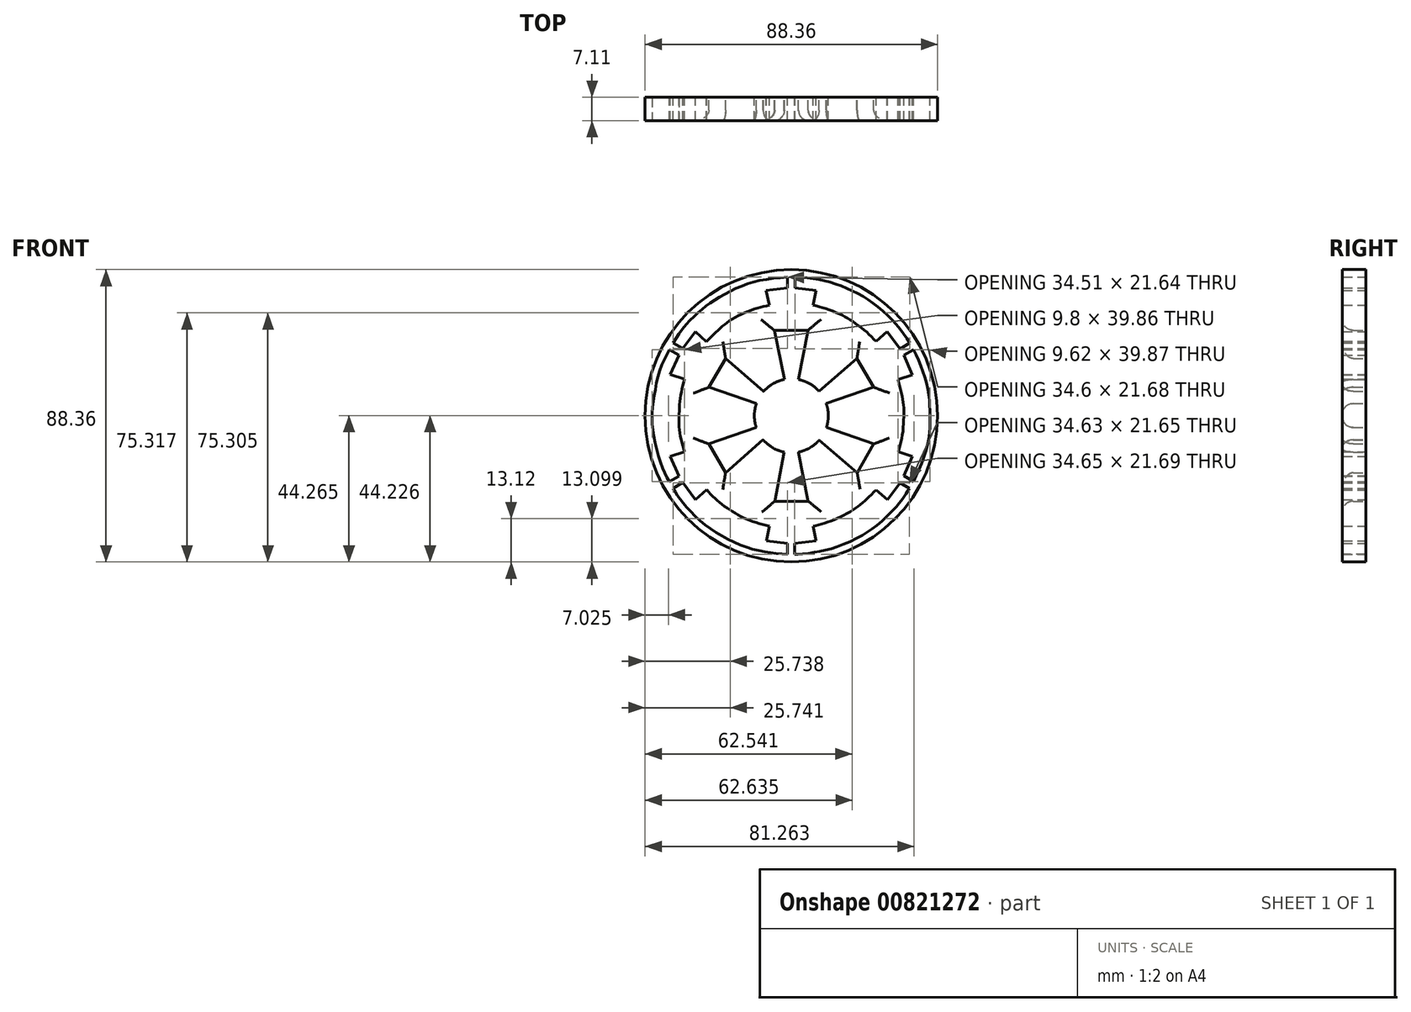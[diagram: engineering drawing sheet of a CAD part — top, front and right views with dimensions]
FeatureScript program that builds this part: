
annotation { "Feature Type Name" : "Feature", "Feature Type Description" : "" }
export const myFeature = defineFeature(function(context is Context, id is Id, definition is map)
    precondition{}
    {
        {
            var Q0;
            Q0=qCreatedBy(makeId("Front.planeOp"),FACE);
            var sketch = newSketch(context, id + "F0", { "sketchPlane" : qUnion([Q0])});
            skLineSegment(sketch, "E0", {"start": v(2.62, -13.26) * mm, "end": v(5.1, -25.8) * mm});
            skLineSegment(sketch, "E1", {"start": v(-2.6, -13.26) * mm, "end": v(-4.96, -25.83) * mm});
            skLineSegment(sketch, "E2", {"start": v(-4.96, -25.83) * mm, "end": v(5.1, -25.8) * mm});
            skLineSegment(sketch, "E3", {"start": v(-10.25, -8.8) * mm, "end": v(-19.88, -17.27) * mm});
            skLineSegment(sketch, "E4", {"start": v(-12.81, -4.3) * mm, "end": v(-24.92, -8.51) * mm});
            skLineSegment(sketch, "E5", {"start": v(-24.92, -8.51) * mm, "end": v(-19.88, -17.27) * mm});
            skLineSegment(sketch, "E6", {"start": v(12.8, -4.3) * mm, "end": v(24.88, -8.51) * mm});
            skLineSegment(sketch, "E7", {"start": v(10.2, -8.87) * mm, "end": v(19.9, -17.2) * mm});
            skLineSegment(sketch, "E8", {"start": v(19.9, -17.2) * mm, "end": v(24.88, -8.51) * mm});
            skLineSegment(sketch, "E9", {"start": v(12.77, 4.44) * mm, "end": v(24.88, 8.63) * mm});
            skLineSegment(sketch, "E10", {"start": v(10.14, 8.94) * mm, "end": v(19.81, 17.33) * mm});
            skLineSegment(sketch, "E11", {"start": v(19.81, 17.33) * mm, "end": v(24.88, 8.63) * mm});
            skLineSegment(sketch, "E12", {"start": v(2.56, 13.27) * mm, "end": v(5.03, 25.86) * mm});
            skLineSegment(sketch, "E13", {"start": v(-2.57, 13.27) * mm, "end": v(-5.14, 25.83) * mm});
            skLineSegment(sketch, "E14", {"start": v(-5.14, 25.83) * mm, "end": v(5.03, 25.86) * mm});
            skLineSegment(sketch, "E15", {"start": v(-10.19, 8.88) * mm, "end": v(-19.85, 17.32) * mm});
            skLineSegment(sketch, "E16", {"start": v(-12.77, 4.43) * mm, "end": v(-24.88, 8.62) * mm});
            skLineSegment(sketch, "E17", {"start": v(-24.88, 8.62) * mm, "end": v(-19.85, 17.32) * mm});
            skLineSegment(sketch, "E18", {"start": v(-1.19, 41.94) * mm, "end": v(-1.19, 38.6) * mm});
            skLineSegment(sketch, "E19", {"start": v(1.15, 41.98) * mm, "end": v(1.15, 38.6) * mm});
            skLineSegment(sketch, "E20", {"start": v(34, 18.3) * mm, "end": v(36.91, 20.02) * mm});
            skLineSegment(sketch, "E21", {"start": v(34, -18.17) * mm, "end": v(36.9, -19.85) * mm});
            skLineSegment(sketch, "E22", {"start": v(32.88, -20.26) * mm, "end": v(35.68, -21.93) * mm});
            skLineSegment(sketch, "E23", {"start": v(-32.81, -20.21) * mm, "end": v(-35.76, -21.87) * mm});
            skLineSegment(sketch, "E24", {"start": v(-36.86, -19.88) * mm, "end": v(-33.93, -18.2) * mm});
            skLineSegment(sketch, "E25", {"start": v(-36.87, 19.98) * mm, "end": v(-33.92, 18.32) * mm});
            skLineSegment(sketch, "E26", {"start": v(-35.7, 22.04) * mm, "end": v(-32.8, 20.3) * mm});
            skLineSegment(sketch, "E27", {"start": v(-33.92, 18.32) * mm, "end": v(-36.56, 12.47) * mm});
            skLineSegment(sketch, "E28", {"start": v(-36.56, 12.47) * mm, "end": v(-32.26, 11.04) * mm});
            skLineSegment(sketch, "E29", {"start": v(-32.8, 20.3) * mm, "end": v(-29, 25.5) * mm});
            skLineSegment(sketch, "E30", {"start": v(-29, 25.5) * mm, "end": v(-25.68, 22.43) * mm});
            skLineSegment(sketch, "E31", {"start": v(-33.93, -18.2) * mm, "end": v(-36.55, -12.33) * mm});
            skLineSegment(sketch, "E32", {"start": v(-36.55, -12.33) * mm, "end": v(-32.26, -10.87) * mm});
            skLineSegment(sketch, "E33", {"start": v(-32.81, -20.21) * mm, "end": v(-28.96, -25.37) * mm});
            skLineSegment(sketch, "E34", {"start": v(-28.96, -25.37) * mm, "end": v(-25.6, -22.34) * mm});
            skPoint(sketch, "E35.end.orphan", {"position": v(-1.27, -41.9) * mm});
            skPoint(sketch, "E35.start.orphan", {"position": v(-1.27, -38.52) * mm});
            skLineSegment(sketch, "E36", {"start": v(-1.12, -38.52) * mm, "end": v(-1.12, -41.9) * mm});
            skPoint(sketch, "E37.end.orphan", {"position": v(1.2, -41.9) * mm});
            skPoint(sketch, "E37.start.orphan", {"position": v(1.2, -38.52) * mm});
            skLineSegment(sketch, "E38", {"start": v(-1.12, -38.52) * mm, "end": v(-1.27, -38.52) * mm});
            skLineSegment(sketch, "E39", {"start": v(-1.12, -38.52) * mm, "end": v(-7.5, -37.75) * mm});
            skLineSegment(sketch, "E40", {"start": v(-7.5, -37.75) * mm, "end": v(-6.57, -33.33) * mm});
            skLineSegment(sketch, "E41", {"start": v(1.04, -38.52) * mm, "end": v(1.04, -41.9) * mm});
            skLineSegment(sketch, "E42", {"start": v(1.04, -38.52) * mm, "end": v(7.43, -37.82) * mm});
            skLineSegment(sketch, "E43", {"start": v(7.43, -37.82) * mm, "end": v(6.52, -33.4) * mm});
            skLineSegment(sketch, "E44", {"start": v(32.88, -20.26) * mm, "end": v(29.04, -25.4) * mm});
            skLineSegment(sketch, "E45", {"start": v(29.04, -25.4) * mm, "end": v(25.6, -22.45) * mm});
            skLineSegment(sketch, "E46", {"start": v(34, -18.17) * mm, "end": v(36.62, -12.34) * mm});
            skLineSegment(sketch, "E47", {"start": v(36.62, -12.34) * mm, "end": v(32.34, -10.9) * mm});
            skLineSegment(sketch, "E48", {"start": v(34, 18.3) * mm, "end": v(36.57, 12.42) * mm});
            skLineSegment(sketch, "E49", {"start": v(36.57, 12.42) * mm, "end": v(32.28, 11.02) * mm});
            skLineSegment(sketch, "E50", {"start": v(32.84, 20.3) * mm, "end": v(35.76, 22) * mm});
            skLineSegment(sketch, "E51", {"start": v(32.84, 20.3) * mm, "end": v(29, 25.44) * mm});
            skLineSegment(sketch, "E52", {"start": v(29, 25.44) * mm, "end": v(25.61, 22.47) * mm});
            skLineSegment(sketch, "E53", {"start": v(-1.19, 38.6) * mm, "end": v(-7.58, 37.87) * mm});
            skLineSegment(sketch, "E54", {"start": v(-7.58, 37.87) * mm, "end": v(-6.6, 33.44) * mm});
            skLineSegment(sketch, "E55", {"start": v(1.15, 38.6) * mm, "end": v(7.53, 37.86) * mm});
            skLineSegment(sketch, "E56", {"start": v(7.53, 37.86) * mm, "end": v(6.59, 33.4) * mm});
            skFitSpline(sketch, "E57", {"points": [v(-32.26, -10.87) * mm, v(-33.66, -5.43) * mm, v(-33.9, 0) * mm, v(-33.54, 5.46) * mm, v(-32.26, 11.04) * mm], "startDerivative": vector(-6.71, 21.57) * mm, "endDerivative": vector(5.92, 22) * mm});
            skFitSpline(sketch, "E58", {"points": [v(-25.68, 22.43) * mm, v(-21.68, 26.27) * mm, v(-17.69, 29.3) * mm, v(-11.76, 32.08) * mm, v(-6.6, 33.44) * mm], "startDerivative": vector(16.19, 16.08) * mm, "endDerivative": vector(20.55, 4.51) * mm});
            skFitSpline(sketch, "E59", {"points": [v(-25.6, -22.34) * mm, v(-22.09, -25.83) * mm, v(-17.7, -29) * mm, v(-12.88, -31.51) * mm, v(-6.57, -33.33) * mm], "startDerivative": vector(14.21, -15.18) * mm, "endDerivative": vector(24.22, -5.87) * mm});
            skFitSpline(sketch, "E60", {"points": [v(6.52, -33.4) * mm, v(10.43, -32.34) * mm, v(15.18, -30.36) * mm, v(19.6, -27.8) * mm, v(22.48, -25.4) * mm, v(25.6, -22.45) * mm], "startDerivative": vector(20.1, 4.76) * mm, "endDerivative": vector(16.26, 15.48) * mm});
            skFitSpline(sketch, "E61", {"points": [v(32.34, -10.9) * mm, v(33.58, -5.53) * mm, v(34, 0) * mm, v(34, 2.2) * mm, v(33.5, 5.84) * mm, v(32.28, 11.02) * mm], "startDerivative": vector(6.39, 22.77) * mm, "endDerivative": vector(-6.09, 23.91) * mm});
            skFitSpline(sketch, "E62", {"points": [v(25.61, 22.47) * mm, v(22.13, 25.84) * mm, v(17.85, 28.97) * mm, v(14.13, 30.98) * mm, v(8.7, 32.92) * mm, v(6.59, 33.4) * mm], "startDerivative": vector(-15.56, 16.18) * mm, "endDerivative": vector(-12.9, 2.5) * mm});
            skFitSpline(sketch, "E63", {"points": [v(-35.7, 22.04) * mm, v(-32.26, 27.01) * mm, v(-27.88, 31.44) * mm, v(-23.76, 34.6) * mm, v(-17.69, 38.04) * mm, v(-10.42, 40.68) * mm, v(-1.19, 41.94) * mm], "startDerivative": vector(20.42, 32.39) * mm, "endDerivative": vector(49.13, 4.55) * mm});
            skFitSpline(sketch, "E64", {"points": [v(-36.87, 19.98) * mm, v(-39.57, 14.2) * mm, v(-41.37, 6.42) * mm, v(-42.05, 0) * mm, v(-41.46, -6.76) * mm, v(-39.1, -15.28) * mm, v(-36.86, -19.88) * mm], "startDerivative": vector(-18.3, -33.84) * mm, "endDerivative": vector(15.88, -28.7) * mm});
            skFitSpline(sketch, "E65", {"points": [v(-35.76, -21.87) * mm, v(-34.07, -24.57) * mm, v(-31.3, -27.99) * mm, v(-26.23, -32.77) * mm, v(-19.88, -36.91) * mm, v(-12.82, -39.98) * mm, v(-6.67, -41.35) * mm, v(-1.12, -41.9) * mm], "startDerivative": vector(15, -25.38) * mm, "endDerivative": vector(39.5, -3.13) * mm});
            skPoint(sketch, "E66.1.internal.orphan", {"position": v(2.81, -41.9) * mm});
            skPoint(sketch, "E66.5.internal.orphan", {"position": v(24.54, -34.16) * mm});
            skPoint(sketch, "E66.7.internal.orphan", {"position": v(32.73, -26.55) * mm});
            skFitSpline(sketch, "E67", {"points": [v(1.04, -41.9) * mm, v(2.34, -41.9) * mm, v(6.1, -41.4) * mm, v(9.9, -40.67) * mm, v(14.23, -39.47) * mm, v(19.53, -37.12) * mm, v(23.68, -34.68) * mm, v(27.2, -31.99) * mm, v(31.17, -28.05) * mm, v(33.22, -25.61) * mm, v(35.68, -21.93) * mm], "startDerivative": vector(19.64, -0.97) * mm, "endDerivative": vector(24.32, 37.94) * mm});
            skFitSpline(sketch, "E68", {"points": [v(1.15, 41.98) * mm, v(8, 41.23) * mm, v(14.33, 39.52) * mm, v(20.7, 36.61) * mm, v(26.6, 32.55) * mm, v(32.17, 27.03) * mm, v(35.76, 22) * mm], "startDerivative": vector(41.76, -3.24) * mm, "endDerivative": vector(20.77, -31.79) * mm});
            skFitSpline(sketch, "E69", {"points": [v(36.91, 20.02) * mm, v(39.69, 13.75) * mm, v(41.52, 6.68) * mm, v(41.88, 1.39) * mm, v(41.79, -4.77) * mm, v(40.16, -12.25) * mm, v(36.9, -19.85) * mm], "startDerivative": vector(17.68, -36.35) * mm, "endDerivative": vector(-19.56, -41.17) * mm});
            skCircle(sketch, "E70", {"center": v(0, 0) * mm, "radius": 44.18 * mm});
            skLineSegment(sketch, "E71", {"start": v(10.56, 3.67) * mm, "end": v(10.5, 3.65) * mm});
            skLineSegment(sketch, "E72", {"start": v(8.37, 7.4) * mm, "end": v(8.32, 7.36) * mm});
            skLineSegment(sketch, "E73", {"start": v(-2.1, 10.98) * mm, "end": v(-2.08, 10.92) * mm});
            skLineSegment(sketch, "E74", {"start": v(2.12, 10.97) * mm, "end": v(2.1, 10.91) * mm});
            skLineSegment(sketch, "E75", {"start": v(-8.42, 7.34) * mm, "end": v(-8.38, 7.3) * mm});
            skLineSegment(sketch, "E76", {"start": v(-10.56, 3.66) * mm, "end": v(-10.5, 3.64) * mm});
            skLineSegment(sketch, "E77", {"start": v(-10.6, -3.52) * mm, "end": v(-10.55, -3.5) * mm});
            skLineSegment(sketch, "E78", {"start": v(-8.5, -7.26) * mm, "end": v(-8.45, -7.22) * mm});
            skLineSegment(sketch, "E79", {"start": v(-2.16, -10.96) * mm, "end": v(-2.15, -10.9) * mm});
            skLineSegment(sketch, "E80", {"start": v(2.17, -10.96) * mm, "end": v(2.16, -10.9) * mm});
            skLineSegment(sketch, "E81", {"start": v(8.42, -7.35) * mm, "end": v(8.37, -7.3) * mm});
            skLineSegment(sketch, "E82", {"start": v(10.6, -3.54) * mm, "end": v(10.54, -3.52) * mm});
            skCircle(sketch, "E83", {"center": v(0, 0) * mm, "radius": 11.18 * mm});
            skLineSegment(sketch, "E84", {"start": v(-10.19, 8.88) * mm, "end": v(-8.42, 7.34) * mm});
            skLineSegment(sketch, "E85", {"start": v(-12.77, 4.43) * mm, "end": v(-10.5, 3.64) * mm});
            skLineSegment(sketch, "E86", {"start": v(-12.81, -4.3) * mm, "end": v(-10.55, -3.5) * mm});
            skLineSegment(sketch, "E87", {"start": v(-10.25, -8.8) * mm, "end": v(-8.45, -7.22) * mm});
            skLineSegment(sketch, "E88", {"start": v(-2.6, -13.26) * mm, "end": v(-2.15, -10.9) * mm});
            skLineSegment(sketch, "E89", {"start": v(2.62, -13.26) * mm, "end": v(2.17, -10.96) * mm});
            skLineSegment(sketch, "E90", {"start": v(10.2, -8.87) * mm, "end": v(8.42, -7.35) * mm});
            skLineSegment(sketch, "E91", {"start": v(12.8, -4.3) * mm, "end": v(10.6, -3.54) * mm});
            skLineSegment(sketch, "E92", {"start": v(12.77, 4.44) * mm, "end": v(10.56, 3.67) * mm});
            skLineSegment(sketch, "E93", {"start": v(10.14, 8.94) * mm, "end": v(8.37, 7.4) * mm});
            skLineSegment(sketch, "E94", {"start": v(2.56, 13.27) * mm, "end": v(2.12, 10.97) * mm});
            skLineSegment(sketch, "E95", {"start": v(-2.57, 13.27) * mm, "end": v(-2.08, 10.92) * mm});
            skSolve(sketch);
        }
        {
            var Q0;
            Q0=qSketchRegion(id+"F0",true);
            extrude(context, id + "F1", {"entities" : qUnion([Q0]), "depth" : 7.11 * mm, "offsetDistance" : 25.4 * mm});
        }
        {
            var Q0;
            Q0=makeQuery(id+"F1.opExtrude","CAP_EDGE",EDGE,{"disambiguationData":[OSD([sQuery(id+"F0.wireOp",EDGE,"E16"),sQuery(id+"F0.wireOp",EDGE,"E85")])],"isStart":false});
            var Q1;
            Q1=makeQuery(id+"F1.opExtrude","CAP_EDGE",EDGE,{"disambiguationData":[OSD([sQuery(id+"F0.wireOp",EDGE,"E4"),sQuery(id+"F0.wireOp",EDGE,"E86")])],"isStart":false});
            var Q2;
            Q2=makeQuery(id+"F1.opExtrude","CAP_EDGE",EDGE,{"disambiguationData":[OSD([sQuery(id+"F0.wireOp",EDGE,"E15"),sQuery(id+"F0.wireOp",EDGE,"E84")])],"isStart":false});
            var Q3;
            Q3=makeQuery(id+"F1.opExtrude","CAP_EDGE",EDGE,{"disambiguationData":[OSD([sQuery(id+"F0.wireOp",EDGE,"E13"),sQuery(id+"F0.wireOp",EDGE,"E95")])],"isStart":false});
            var Q4;
            Q4=makeQuery(id+"F1.opExtrude","CAP_EDGE",EDGE,{"disambiguationData":[OSD([sQuery(id+"F0.wireOp",EDGE,"E12"),sQuery(id+"F0.wireOp",EDGE,"E94")])],"isStart":false});
            var Q5;
            Q5=makeQuery(id+"F1.opExtrude","CAP_EDGE",EDGE,{"disambiguationData":[OSD([sQuery(id+"F0.wireOp",EDGE,"E10"),sQuery(id+"F0.wireOp",EDGE,"E93")])],"isStart":false});
            var Q6;
            Q6=makeQuery(id+"F1.opExtrude","CAP_EDGE",EDGE,{"disambiguationData":[OSD([sQuery(id+"F0.wireOp",EDGE,"E9"),sQuery(id+"F0.wireOp",EDGE,"E92")])],"isStart":false});
            var Q7;
            Q7=makeQuery(id+"F1.opExtrude","CAP_EDGE",EDGE,{"disambiguationData":[OSD([sQuery(id+"F0.wireOp",EDGE,"E6"),sQuery(id+"F0.wireOp",EDGE,"E91")])],"isStart":false});
            var Q8;
            Q8=makeQuery(id+"F1.opExtrude","CAP_EDGE",EDGE,{"disambiguationData":[OSD([sQuery(id+"F0.wireOp",EDGE,"E7"),sQuery(id+"F0.wireOp",EDGE,"E90")])],"isStart":false});
            var Q9;
            Q9=makeQuery(id+"F1.opExtrude","CAP_EDGE",EDGE,{"disambiguationData":[OSD([sQuery(id+"F0.wireOp",EDGE,"E0"),sQuery(id+"F0.wireOp",EDGE,"E89")])],"isStart":false});
            var Q10;
            Q10=makeQuery(id+"F1.opExtrude","CAP_EDGE",EDGE,{"disambiguationData":[OSD([sQuery(id+"F0.wireOp",EDGE,"E3"),sQuery(id+"F0.wireOp",EDGE,"E87")])],"isStart":false});
            var Q11;
            Q11=makeQuery(id+"F1.opExtrude","CAP_EDGE",EDGE,{"disambiguationData":[OSD([sQuery(id+"F0.wireOp",EDGE,"E1"),sQuery(id+"F0.wireOp",EDGE,"E88")])],"isStart":false});
            var Q12;
            Q12=makeQuery(id+"F1.opExtrude","CAP_EDGE",EDGE,{"disambiguationData":[OSD([sQuery(id+"F0.wireOp",EDGE,"E2")])],"isStart":false});
            var Q13;
            Q13=makeQuery(id+"F1.opExtrude","CAP_EDGE",EDGE,{"disambiguationData":[OSD([sQuery(id+"F0.wireOp",EDGE,"E5")])],"isStart":false});
            var Q14;
            Q14=makeQuery(id+"F1.opExtrude","CAP_EDGE",EDGE,{"disambiguationData":[OSD([sQuery(id+"F0.wireOp",EDGE,"E17")])],"isStart":false});
            var Q15;
            Q15=makeQuery(id+"F1.opExtrude","CAP_EDGE",EDGE,{"disambiguationData":[OSD([sQuery(id+"F0.wireOp",EDGE,"E14")])],"isStart":false});
            var Q16;
            Q16=makeQuery(id+"F1.opExtrude","CAP_EDGE",EDGE,{"disambiguationData":[OSD([sQuery(id+"F0.wireOp",EDGE,"E11")])],"isStart":false});
            var Q17;
            Q17=makeQuery(id+"F1.opExtrude","CAP_EDGE",EDGE,{"disambiguationData":[OSD([sQuery(id+"F0.wireOp",EDGE,"E8")])],"isStart":false});
            fillet(context, id + "F2", {"entities" : qUnion([Q0, Q1, Q2, Q3, Q4, Q5, Q6, Q7, Q8, Q9, Q10, Q11, Q12, Q13, Q14, Q15, Q16, Q17]), "radius" : 3.24 * mm, "tangentPropagation" : true, "allowEdgeOverflow" : false});
        }
    });
